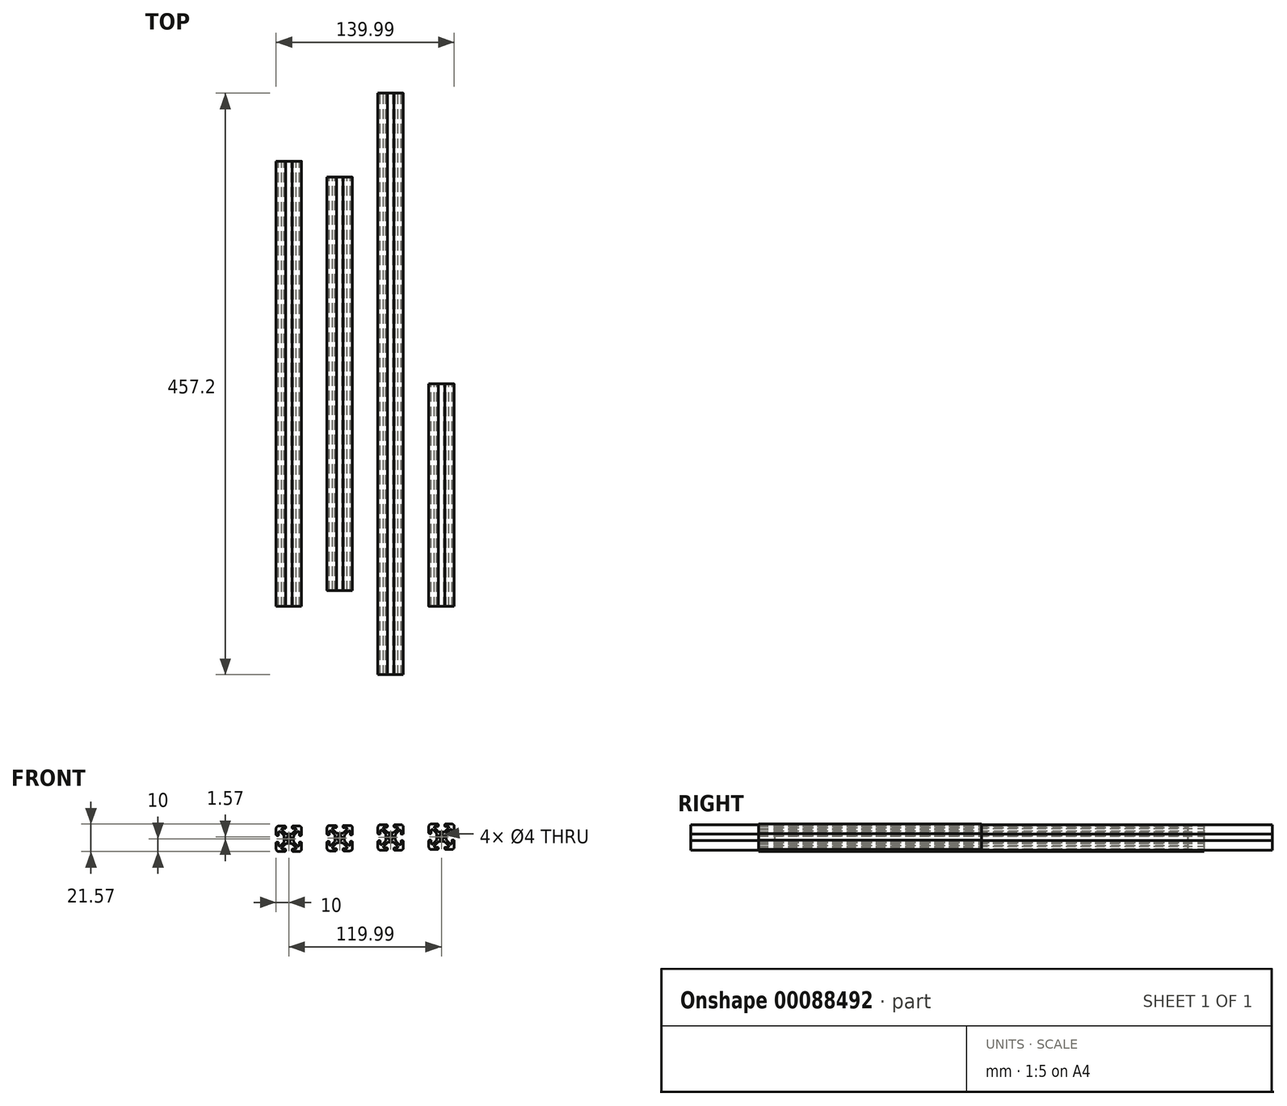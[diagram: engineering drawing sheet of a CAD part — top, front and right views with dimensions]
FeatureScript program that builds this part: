
annotation { "Feature Type Name" : "Feature", "Feature Type Description" : "" }
export const myFeature = defineFeature(function(context is Context, id is Id, definition is map)
    precondition{}
    {
        {
            var Q0;
            Q0=qCreatedBy(makeId("Front.planeOp"),FACE);
            var sketch = newSketch(context, id + "F0", { "sketchPlane" : qUnion([Q0])});
            skLineSegment(sketch, "E0.0.53", {"start": v(3.64, 0) * mm, "end": v(3.64, 1.13) * mm});
            skArc(sketch, "E0.0.54", {"start": v(3.64, 1.13) * mm, "mid": v(3.87, 2.28) * mm, "end": v(4.52, 3.25) * mm});
            skLineSegment(sketch, "E0.0.55", {"start": v(4.52, 3.25) * mm, "end": v(6.77, 5.5) * mm});
            skArc(sketch, "E0.0.56", {"start": v(6.77, 5.5) * mm, "mid": v(7.68, 5.68) * mm, "end": v(8.2, 4.9) * mm});
            skLineSegment(sketch, "E0.0.57", {"start": v(8.2, 4.9) * mm, "end": v(8.2, 2.8) * mm});
            skArc(sketch, "E0.0.58", {"start": v(8.2, 2.8) * mm, "mid": v(8.29, 2.59) * mm, "end": v(8.5, 2.5) * mm});
            skLineSegment(sketch, "E0.0.59", {"start": v(8.5, 2.5) * mm, "end": v(9.21, 2.5) * mm});
            skArc(sketch, "E0.0.60", {"start": v(9.21, 2.5) * mm, "mid": v(9.77, 2.73) * mm, "end": v(10, 3.29) * mm});
            skLineSegment(sketch, "E0.0.61", {"start": v(10, 3.29) * mm, "end": v(10, 7.99) * mm});
            skArc(sketch, "E0.0.62", {"start": v(10, 7.99) * mm, "mid": v(9.41, 9.41) * mm, "end": v(7.99, 10) * mm});
            skLineSegment(sketch, "E0.0.63", {"start": v(7.99, 10) * mm, "end": v(3.29, 10) * mm});
            skArc(sketch, "E0.0.64", {"start": v(3.29, 10) * mm, "mid": v(2.73, 9.77) * mm, "end": v(2.5, 9.21) * mm});
            skLineSegment(sketch, "E0.0.65", {"start": v(2.5, 9.21) * mm, "end": v(2.5, 8.5) * mm});
            skArc(sketch, "E0.0.66", {"start": v(2.5, 8.5) * mm, "mid": v(2.59, 8.29) * mm, "end": v(2.8, 8.2) * mm});
            skLineSegment(sketch, "E0.0.67", {"start": v(2.8, 8.2) * mm, "end": v(4.9, 8.2) * mm});
            skArc(sketch, "E0.0.68", {"start": v(4.9, 8.2) * mm, "mid": v(5.68, 7.68) * mm, "end": v(5.5, 6.77) * mm});
            skLineSegment(sketch, "E0.0.69", {"start": v(5.5, 6.77) * mm, "end": v(3.25, 4.52) * mm});
            skArc(sketch, "E0.0.70", {"start": v(3.25, 4.52) * mm, "mid": v(2.28, 3.87) * mm, "end": v(1.13, 3.64) * mm});
            skLineSegment(sketch, "E0.0.71", {"start": v(1.13, 3.64) * mm, "end": v(0, 3.64) * mm});
            skLineSegment(sketch, "E1", {"start": v(0, 0) * mm, "end": v(0, 10.71) * mm, "construction": true});
            skLineSegment(sketch, "E2", {"start": v(0, 0) * mm, "end": v(12.42, 0) * mm, "construction": true});
            skLineSegment(sketch, "E3", {"start": v(0, 0) * mm, "end": v(7.99, 7.99) * mm, "construction": true});
            skLineSegment(sketch, "E4.MirrorCS", {"start": v(8.5, -2.5) * mm, "end": v(9.21, -2.5) * mm});
            skArc(sketch, "E5.MirrorCS", {"start": v(8.2, -2.8) * mm, "mid": v(8.29, -2.59) * mm, "end": v(8.5, -2.5) * mm});
            skArc(sketch, "E6.MirrorCS", {"start": v(2.5, -8.5) * mm, "mid": v(2.59, -8.29) * mm, "end": v(2.8, -8.2) * mm});
            skLineSegment(sketch, "E7.MirrorCS", {"start": v(2.5, -9.21) * mm, "end": v(2.5, -8.5) * mm});
            skArc(sketch, "E8.MirrorCS", {"start": v(4.9, -8.2) * mm, "mid": v(5.68, -7.68) * mm, "end": v(5.5, -6.77) * mm});
            skArc(sketch, "E9.MirrorCS", {"start": v(3.64, -1.13) * mm, "mid": v(3.87, -2.28) * mm, "end": v(4.52, -3.25) * mm});
            skLineSegment(sketch, "E10.MirrorCS", {"start": v(10, -3.29) * mm, "end": v(10, -7.99) * mm});
            skArc(sketch, "E11.MirrorCS", {"start": v(3.25, -4.52) * mm, "mid": v(2.28, -3.87) * mm, "end": v(1.13, -3.64) * mm});
            skArc(sketch, "E12.MirrorCS", {"start": v(9.21, -2.5) * mm, "mid": v(9.77, -2.73) * mm, "end": v(10, -3.29) * mm});
            skLineSegment(sketch, "E13.MirrorCS", {"start": v(2.8, -8.2) * mm, "end": v(4.9, -8.2) * mm});
            skLineSegment(sketch, "E14.MirrorCS", {"start": v(4.52, -3.25) * mm, "end": v(6.77, -5.5) * mm});
            skLineSegment(sketch, "E15.MirrorCS", {"start": v(8.2, -4.9) * mm, "end": v(8.2, -2.8) * mm});
            skLineSegment(sketch, "E16.MirrorCS", {"start": v(3.64, 0) * mm, "end": v(3.64, -1.13) * mm});
            skLineSegment(sketch, "E17.MirrorCS", {"start": v(7.99, -10) * mm, "end": v(3.29, -10) * mm});
            skLineSegment(sketch, "E18.MirrorCS", {"start": v(5.5, -6.77) * mm, "end": v(3.25, -4.52) * mm});
            skArc(sketch, "E19.MirrorCS", {"start": v(6.77, -5.5) * mm, "mid": v(7.68, -5.68) * mm, "end": v(8.2, -4.9) * mm});
            skArc(sketch, "E20.MirrorCS", {"start": v(10, -7.99) * mm, "mid": v(9.41, -9.41) * mm, "end": v(7.99, -10) * mm});
            skArc(sketch, "E21.MirrorCS", {"start": v(3.29, -10) * mm, "mid": v(2.73, -9.77) * mm, "end": v(2.5, -9.21) * mm});
            skLineSegment(sketch, "E22.MirrorCS", {"start": v(1.13, -3.64) * mm, "end": v(0, -3.64) * mm});
            skLineSegment(sketch, "E23.MirrorCS", {"start": v(-2.5, 9.21) * mm, "end": v(-2.5, 8.5) * mm});
            skArc(sketch, "E24.MirrorCS", {"start": v(-8.2, -2.8) * mm, "mid": v(-8.29, -2.59) * mm, "end": v(-8.5, -2.5) * mm});
            skLineSegment(sketch, "E25.MirrorCS", {"start": v(-8.5, -2.5) * mm, "end": v(-9.21, -2.5) * mm});
            skArc(sketch, "E26.MirrorCS", {"start": v(-2.5, 8.5) * mm, "mid": v(-2.59, 8.29) * mm, "end": v(-2.8, 8.2) * mm});
            skLineSegment(sketch, "E27.MirrorCS", {"start": v(-3.64, 0) * mm, "end": v(-3.64, 1.13) * mm});
            skLineSegment(sketch, "E28.MirrorCS", {"start": v(-3.64, 0) * mm, "end": v(-3.64, -1.13) * mm});
            skArc(sketch, "E29.MirrorCS", {"start": v(-2.5, -8.5) * mm, "mid": v(-2.59, -8.29) * mm, "end": v(-2.8, -8.2) * mm});
            skLineSegment(sketch, "E30.MirrorCS", {"start": v(-2.5, -9.21) * mm, "end": v(-2.5, -8.5) * mm});
            skLineSegment(sketch, "E31.MirrorCS", {"start": v(-8.5, 2.5) * mm, "end": v(-9.21, 2.5) * mm});
            skArc(sketch, "E32.MirrorCS", {"start": v(-8.2, 2.8) * mm, "mid": v(-8.29, 2.59) * mm, "end": v(-8.5, 2.5) * mm});
            skLineSegment(sketch, "E33.MirrorCS", {"start": v(-1.13, -3.64) * mm, "end": v(0, -3.64) * mm});
            skLineSegment(sketch, "E34.MirrorCS", {"start": v(-1.13, 3.64) * mm, "end": v(0, 3.64) * mm});
            skArc(sketch, "E35.MirrorCS", {"start": v(-9.21, -2.5) * mm, "mid": v(-9.77, -2.73) * mm, "end": v(-10, -3.29) * mm});
            skLineSegment(sketch, "E36.MirrorCS", {"start": v(-4.52, 3.25) * mm, "end": v(-6.77, 5.5) * mm});
            skLineSegment(sketch, "E37.MirrorCS", {"start": v(-5.5, 6.77) * mm, "end": v(-3.25, 4.52) * mm});
            skLineSegment(sketch, "E38.MirrorCS", {"start": v(-8.2, 4.9) * mm, "end": v(-8.2, 2.8) * mm});
            skArc(sketch, "E39.MirrorCS", {"start": v(-6.77, 5.5) * mm, "mid": v(-7.68, 5.68) * mm, "end": v(-8.2, 4.9) * mm});
            skArc(sketch, "E40.MirrorCS", {"start": v(-4.9, -8.2) * mm, "mid": v(-5.68, -7.68) * mm, "end": v(-5.5, -6.77) * mm});
            skLineSegment(sketch, "E41.MirrorCS", {"start": v(-7.99, -10) * mm, "end": v(-3.29, -10) * mm});
            skArc(sketch, "E42.MirrorCS", {"start": v(-3.25, 4.52) * mm, "mid": v(-2.28, 3.87) * mm, "end": v(-1.13, 3.64) * mm});
            skArc(sketch, "E43.MirrorCS", {"start": v(-6.77, -5.5) * mm, "mid": v(-7.68, -5.68) * mm, "end": v(-8.2, -4.9) * mm});
            skLineSegment(sketch, "E44.MirrorCS", {"start": v(-2.8, -8.2) * mm, "end": v(-4.9, -8.2) * mm});
            skArc(sketch, "E45.MirrorCS", {"start": v(-3.25, -4.52) * mm, "mid": v(-2.28, -3.87) * mm, "end": v(-1.13, -3.64) * mm});
            skArc(sketch, "E46.MirrorCS", {"start": v(-3.64, -1.13) * mm, "mid": v(-3.87, -2.28) * mm, "end": v(-4.52, -3.25) * mm});
            skLineSegment(sketch, "E47.MirrorCS", {"start": v(-2.8, 8.2) * mm, "end": v(-4.9, 8.2) * mm});
            skArc(sketch, "E48.MirrorCS", {"start": v(-4.9, 8.2) * mm, "mid": v(-5.68, 7.68) * mm, "end": v(-5.5, 6.77) * mm});
            skLineSegment(sketch, "E49.MirrorCS", {"start": v(-10, -3.29) * mm, "end": v(-10, -7.99) * mm});
            skArc(sketch, "E50.MirrorCS", {"start": v(-3.29, -10) * mm, "mid": v(-2.73, -9.77) * mm, "end": v(-2.5, -9.21) * mm});
            skArc(sketch, "E51.MirrorCS", {"start": v(-10, -7.99) * mm, "mid": v(-9.41, -9.41) * mm, "end": v(-7.99, -10) * mm});
            skArc(sketch, "E52.MirrorCS", {"start": v(-3.29, 10) * mm, "mid": v(-2.73, 9.77) * mm, "end": v(-2.5, 9.21) * mm});
            skLineSegment(sketch, "E53.MirrorCS", {"start": v(-7.99, 10) * mm, "end": v(-3.29, 10) * mm});
            skArc(sketch, "E54.MirrorCS", {"start": v(-10, 7.99) * mm, "mid": v(-9.41, 9.41) * mm, "end": v(-7.99, 10) * mm});
            skLineSegment(sketch, "E55.MirrorCS", {"start": v(-8.2, -4.9) * mm, "end": v(-8.2, -2.8) * mm});
            skArc(sketch, "E56.MirrorCS", {"start": v(-3.64, 1.13) * mm, "mid": v(-3.87, 2.28) * mm, "end": v(-4.52, 3.25) * mm});
            skLineSegment(sketch, "E57.MirrorCS", {"start": v(-5.5, -6.77) * mm, "end": v(-3.25, -4.52) * mm});
            skLineSegment(sketch, "E58.MirrorCS", {"start": v(-10, 3.29) * mm, "end": v(-10, 7.99) * mm});
            skArc(sketch, "E59.MirrorCS", {"start": v(-9.21, 2.5) * mm, "mid": v(-9.77, 2.73) * mm, "end": v(-10, 3.29) * mm});
            skLineSegment(sketch, "E60.MirrorCS", {"start": v(-4.52, -3.25) * mm, "end": v(-6.77, -5.5) * mm});
            skCircle(sketch, "E61", {"center": v(0, 0) * mm, "radius": 2 * mm});
            skArc(sketch, "E62.1.0.0", {"start": v(44.9, -7.68) * mm, "mid": v(45.68, -7.16) * mm, "end": v(45.5, -6.25) * mm});
            skArc(sketch, "E62.1.0.1", {"start": v(36.35, 1.65) * mm, "mid": v(36.12, 2.8) * mm, "end": v(35.47, 3.77) * mm});
            skLineSegment(sketch, "E62.1.0.2", {"start": v(40, 0.52) * mm, "end": v(40, 11.24) * mm, "construction": true});
            skLineSegment(sketch, "E62.1.0.3", {"start": v(30, -2.76) * mm, "end": v(30, -7.46) * mm});
            skLineSegment(sketch, "E62.1.0.4", {"start": v(47.98, -9.48) * mm, "end": v(43.28, -9.48) * mm});
            skLineSegment(sketch, "E62.1.0.5", {"start": v(32, -9.48) * mm, "end": v(36.7, -9.48) * mm});
            skArc(sketch, "E62.1.0.6", {"start": v(43.64, -0.6) * mm, "mid": v(43.87, -1.75) * mm, "end": v(44.52, -2.73) * mm});
            skLineSegment(sketch, "E62.1.0.7", {"start": v(34.5, -6.25) * mm, "end": v(36.75, -4) * mm});
            skLineSegment(sketch, "E62.1.0.8", {"start": v(40, 0.52) * mm, "end": v(52.42, 0.52) * mm, "construction": true});
            skArc(sketch, "E62.1.0.9", {"start": v(33.22, -4.98) * mm, "mid": v(32.31, -5.16) * mm, "end": v(31.8, -4.39) * mm});
            skLineSegment(sketch, "E62.1.0.10", {"start": v(45.5, -6.25) * mm, "end": v(43.25, -4) * mm});
            skArc(sketch, "E62.1.0.11", {"start": v(43.25, -4) * mm, "mid": v(42.27, -3.35) * mm, "end": v(41.13, -3.12) * mm});
            skArc(sketch, "E62.1.0.12", {"start": v(36.75, 5.05) * mm, "mid": v(37.72, 4.4) * mm, "end": v(38.87, 4.17) * mm});
            skLineSegment(sketch, "E62.1.0.13", {"start": v(50, -2.76) * mm, "end": v(50, -7.46) * mm});
            skLineSegment(sketch, "E62.1.0.14", {"start": v(30, 3.81) * mm, "end": v(30, 8.51) * mm});
            skLineSegment(sketch, "E62.1.0.15", {"start": v(40, 0.52) * mm, "end": v(47.98, 8.51) * mm, "construction": true});
            skLineSegment(sketch, "E62.1.0.16", {"start": v(35.47, -2.73) * mm, "end": v(33.22, -4.98) * mm});
            skArc(sketch, "E62.1.0.17", {"start": v(30, -7.46) * mm, "mid": v(30.59, -8.89) * mm, "end": v(32, -9.48) * mm});
            skLineSegment(sketch, "E62.1.0.18", {"start": v(37.2, -7.68) * mm, "end": v(35.09, -7.68) * mm});
            skCircle(sketch, "E62.1.0.19", {"center": v(40, 0.52) * mm, "radius": 2 * mm});
            skArc(sketch, "E62.1.0.20", {"start": v(36.75, -4) * mm, "mid": v(37.72, -3.35) * mm, "end": v(38.87, -3.12) * mm});
            skLineSegment(sketch, "E62.1.0.21", {"start": v(35.47, 3.77) * mm, "end": v(33.22, 6.02) * mm});
            skArc(sketch, "E62.1.0.22", {"start": v(50, -7.46) * mm, "mid": v(49.4, -8.89) * mm, "end": v(47.98, -9.48) * mm});
            skLineSegment(sketch, "E62.1.0.23", {"start": v(42.8, -7.68) * mm, "end": v(44.9, -7.68) * mm});
            skLineSegment(sketch, "E62.1.0.24", {"start": v(42.8, 8.72) * mm, "end": v(44.9, 8.72) * mm});
            skArc(sketch, "E62.1.0.25", {"start": v(44.9, 8.72) * mm, "mid": v(45.68, 8.2) * mm, "end": v(45.5, 7.3) * mm});
            skArc(sketch, "E62.1.0.26", {"start": v(43.64, 1.65) * mm, "mid": v(43.87, 2.8) * mm, "end": v(44.52, 3.77) * mm});
            skLineSegment(sketch, "E62.1.0.27", {"start": v(44.52, 3.77) * mm, "end": v(46.77, 6.02) * mm});
            skLineSegment(sketch, "E62.1.0.28", {"start": v(48.2, 5.43) * mm, "end": v(48.2, 3.33) * mm});
            skLineSegment(sketch, "E62.1.0.29", {"start": v(50, 3.81) * mm, "end": v(50, 8.51) * mm});
            skArc(sketch, "E62.1.0.30", {"start": v(50, 8.51) * mm, "mid": v(49.4, 9.93) * mm, "end": v(47.98, 10.52) * mm});
            skLineSegment(sketch, "E62.1.0.31", {"start": v(47.98, 10.52) * mm, "end": v(43.28, 10.52) * mm});
            skLineSegment(sketch, "E62.1.0.32", {"start": v(34.5, 7.3) * mm, "end": v(36.75, 5.05) * mm});
            skLineSegment(sketch, "E62.1.0.33", {"start": v(32, 10.52) * mm, "end": v(36.7, 10.52) * mm});
            skLineSegment(sketch, "E62.1.0.34", {"start": v(45.5, 7.3) * mm, "end": v(43.25, 5.05) * mm});
            skLineSegment(sketch, "E62.1.0.35", {"start": v(44.52, -2.73) * mm, "end": v(46.77, -4.98) * mm});
            skLineSegment(sketch, "E62.1.0.36", {"start": v(31.8, 5.43) * mm, "end": v(31.8, 3.33) * mm});
            skArc(sketch, "E62.1.0.37", {"start": v(30, 8.51) * mm, "mid": v(30.59, 9.93) * mm, "end": v(32, 10.52) * mm});
            skArc(sketch, "E62.1.0.38", {"start": v(43.25, 5.05) * mm, "mid": v(42.27, 4.4) * mm, "end": v(41.13, 4.17) * mm});
            skLineSegment(sketch, "E62.1.0.39", {"start": v(48.2, -4.39) * mm, "end": v(48.2, -2.28) * mm});
            skArc(sketch, "E62.1.0.40", {"start": v(33.22, 6.02) * mm, "mid": v(32.31, 6.2) * mm, "end": v(31.8, 5.43) * mm});
            skLineSegment(sketch, "E62.1.0.41", {"start": v(31.8, -4.39) * mm, "end": v(31.8, -2.28) * mm});
            skArc(sketch, "E62.1.0.42", {"start": v(36.35, -0.6) * mm, "mid": v(36.12, -1.75) * mm, "end": v(35.47, -2.73) * mm});
            skLineSegment(sketch, "E62.1.0.43", {"start": v(37.2, 8.72) * mm, "end": v(35.09, 8.72) * mm});
            skArc(sketch, "E62.1.0.44", {"start": v(35.09, -7.68) * mm, "mid": v(34.32, -7.16) * mm, "end": v(34.5, -6.25) * mm});
            skArc(sketch, "E62.1.0.45", {"start": v(31.8, -2.28) * mm, "mid": v(31.7, -2.07) * mm, "end": v(31.5, -1.98) * mm});
            skLineSegment(sketch, "E62.1.0.46", {"start": v(38.87, -3.12) * mm, "end": v(40, -3.12) * mm});
            skLineSegment(sketch, "E62.1.0.47", {"start": v(31.5, -1.98) * mm, "end": v(30.78, -1.98) * mm});
            skArc(sketch, "E62.1.0.48", {"start": v(30.78, 3.02) * mm, "mid": v(30.23, 3.25) * mm, "end": v(30, 3.81) * mm});
            skArc(sketch, "E62.1.0.49", {"start": v(36.7, -9.48) * mm, "mid": v(37.27, -9.25) * mm, "end": v(37.5, -8.69) * mm});
            skLineSegment(sketch, "E62.1.0.50", {"start": v(38.87, 4.17) * mm, "end": v(40, 4.17) * mm});
            skLineSegment(sketch, "E62.1.0.51", {"start": v(36.35, 0.52) * mm, "end": v(36.35, 1.65) * mm});
            skArc(sketch, "E62.1.0.52", {"start": v(30.78, -1.98) * mm, "mid": v(30.23, -2.2) * mm, "end": v(30, -2.76) * mm});
            skLineSegment(sketch, "E62.1.0.53", {"start": v(36.35, 0.52) * mm, "end": v(36.35, -0.6) * mm});
            skArc(sketch, "E62.1.0.54", {"start": v(46.77, -4.98) * mm, "mid": v(47.68, -5.16) * mm, "end": v(48.2, -4.39) * mm});
            skArc(sketch, "E62.1.0.55", {"start": v(49.2, -1.98) * mm, "mid": v(49.77, -2.2) * mm, "end": v(50, -2.76) * mm});
            skArc(sketch, "E62.1.0.56", {"start": v(36.7, 10.52) * mm, "mid": v(37.27, 10.3) * mm, "end": v(37.5, 9.74) * mm});
            skArc(sketch, "E62.1.0.57", {"start": v(37.5, -7.98) * mm, "mid": v(37.4, -7.77) * mm, "end": v(37.2, -7.68) * mm});
            skLineSegment(sketch, "E62.1.0.58", {"start": v(43.64, 0.52) * mm, "end": v(43.64, 1.65) * mm});
            skArc(sketch, "E62.1.0.59", {"start": v(46.77, 6.02) * mm, "mid": v(47.68, 6.2) * mm, "end": v(48.2, 5.43) * mm});
            skArc(sketch, "E62.1.0.60", {"start": v(48.2, 3.33) * mm, "mid": v(48.29, 3.11) * mm, "end": v(48.5, 3.02) * mm});
            skLineSegment(sketch, "E62.1.0.61", {"start": v(48.5, 3.02) * mm, "end": v(49.2, 3.02) * mm});
            skArc(sketch, "E62.1.0.62", {"start": v(49.2, 3.02) * mm, "mid": v(49.77, 3.25) * mm, "end": v(50, 3.81) * mm});
            skArc(sketch, "E62.1.0.63", {"start": v(43.28, 10.52) * mm, "mid": v(42.73, 10.3) * mm, "end": v(42.5, 9.74) * mm});
            skArc(sketch, "E62.1.0.64", {"start": v(43.28, -9.48) * mm, "mid": v(42.73, -9.25) * mm, "end": v(42.5, -8.69) * mm});
            skArc(sketch, "E62.1.0.65", {"start": v(48.2, -2.28) * mm, "mid": v(48.29, -2.07) * mm, "end": v(48.5, -1.98) * mm});
            skLineSegment(sketch, "E62.1.0.66", {"start": v(37.5, -8.69) * mm, "end": v(37.5, -7.98) * mm});
            skLineSegment(sketch, "E62.1.0.67", {"start": v(41.13, -3.12) * mm, "end": v(40, -3.12) * mm});
            skArc(sketch, "E62.1.0.68", {"start": v(42.5, -7.98) * mm, "mid": v(42.59, -7.77) * mm, "end": v(42.8, -7.68) * mm});
            skLineSegment(sketch, "E62.1.0.69", {"start": v(31.5, 3.02) * mm, "end": v(30.78, 3.02) * mm});
            skLineSegment(sketch, "E62.1.0.70", {"start": v(42.5, -8.69) * mm, "end": v(42.5, -7.98) * mm});
            skLineSegment(sketch, "E62.1.0.71", {"start": v(41.13, 4.17) * mm, "end": v(40, 4.17) * mm});
            skArc(sketch, "E62.1.0.72", {"start": v(35.09, 8.72) * mm, "mid": v(34.32, 8.2) * mm, "end": v(34.5, 7.3) * mm});
            skArc(sketch, "E62.1.0.73", {"start": v(31.8, 3.33) * mm, "mid": v(31.7, 3.11) * mm, "end": v(31.5, 3.02) * mm});
            skLineSegment(sketch, "E62.1.0.74", {"start": v(43.64, 0.52) * mm, "end": v(43.64, -0.6) * mm});
            skArc(sketch, "E62.1.0.75", {"start": v(37.5, 9.03) * mm, "mid": v(37.4, 8.81) * mm, "end": v(37.2, 8.72) * mm});
            skLineSegment(sketch, "E62.1.0.76", {"start": v(48.5, -1.98) * mm, "end": v(49.2, -1.98) * mm});
            skArc(sketch, "E62.1.0.77", {"start": v(42.5, 9.03) * mm, "mid": v(42.59, 8.81) * mm, "end": v(42.8, 8.72) * mm});
            skLineSegment(sketch, "E62.1.0.78", {"start": v(42.5, 9.74) * mm, "end": v(42.5, 9.03) * mm});
            skLineSegment(sketch, "E62.1.0.79", {"start": v(37.5, 9.74) * mm, "end": v(37.5, 9.03) * mm});
            skArc(sketch, "E62.2.0.0", {"start": v(84.9, -7.15) * mm, "mid": v(85.67, -6.64) * mm, "end": v(85.5, -5.73) * mm});
            skArc(sketch, "E62.2.0.1", {"start": v(76.35, 2.18) * mm, "mid": v(76.12, 3.32) * mm, "end": v(75.47, 4.3) * mm});
            skLineSegment(sketch, "E62.2.0.2", {"start": v(80, 1.05) * mm, "end": v(80, 11.76) * mm, "construction": true});
            skLineSegment(sketch, "E62.2.0.3", {"start": v(70, -2.24) * mm, "end": v(70, -6.94) * mm});
            skLineSegment(sketch, "E62.2.0.4", {"start": v(87.98, -8.95) * mm, "end": v(83.28, -8.95) * mm});
            skLineSegment(sketch, "E62.2.0.5", {"start": v(72, -8.95) * mm, "end": v(76.7, -8.95) * mm});
            skArc(sketch, "E62.2.0.6", {"start": v(83.64, -0.08) * mm, "mid": v(83.87, -1.23) * mm, "end": v(84.52, -2.2) * mm});
            skLineSegment(sketch, "E62.2.0.7", {"start": v(74.5, -5.73) * mm, "end": v(76.74, -3.48) * mm});
            skLineSegment(sketch, "E62.2.0.8", {"start": v(80, 1.05) * mm, "end": v(92.41, 1.05) * mm, "construction": true});
            skArc(sketch, "E62.2.0.9", {"start": v(73.22, -4.45) * mm, "mid": v(72.3, -4.63) * mm, "end": v(71.8, -3.86) * mm});
            skLineSegment(sketch, "E62.2.0.10", {"start": v(85.5, -5.73) * mm, "end": v(83.24, -3.48) * mm});
            skArc(sketch, "E62.2.0.11", {"start": v(83.24, -3.48) * mm, "mid": v(82.27, -2.83) * mm, "end": v(81.12, -2.6) * mm});
            skArc(sketch, "E62.2.0.12", {"start": v(76.74, 5.57) * mm, "mid": v(77.72, 4.92) * mm, "end": v(78.86, 4.7) * mm});
            skLineSegment(sketch, "E62.2.0.13", {"start": v(90, -2.24) * mm, "end": v(90, -6.94) * mm});
            skLineSegment(sketch, "E62.2.0.14", {"start": v(70, 4.33) * mm, "end": v(70, 9.03) * mm});
            skLineSegment(sketch, "E62.2.0.15", {"start": v(80, 1.05) * mm, "end": v(87.98, 9.03) * mm, "construction": true});
            skLineSegment(sketch, "E62.2.0.16", {"start": v(75.47, -2.2) * mm, "end": v(73.22, -4.45) * mm});
            skArc(sketch, "E62.2.0.17", {"start": v(70, -6.94) * mm, "mid": v(70.58, -8.36) * mm, "end": v(72, -8.95) * mm});
            skLineSegment(sketch, "E62.2.0.18", {"start": v(77.19, -7.15) * mm, "end": v(75.08, -7.15) * mm});
            skCircle(sketch, "E62.2.0.19", {"center": v(80, 1.05) * mm, "radius": 2 * mm});
            skArc(sketch, "E62.2.0.20", {"start": v(76.74, -3.48) * mm, "mid": v(77.72, -2.83) * mm, "end": v(78.86, -2.6) * mm});
            skLineSegment(sketch, "E62.2.0.21", {"start": v(75.47, 4.3) * mm, "end": v(73.22, 6.55) * mm});
            skArc(sketch, "E62.2.0.22", {"start": v(90, -6.94) * mm, "mid": v(89.4, -8.36) * mm, "end": v(87.98, -8.95) * mm});
            skLineSegment(sketch, "E62.2.0.23", {"start": v(82.8, -7.15) * mm, "end": v(84.9, -7.15) * mm});
            skLineSegment(sketch, "E62.2.0.24", {"start": v(82.8, 9.25) * mm, "end": v(84.9, 9.25) * mm});
            skArc(sketch, "E62.2.0.25", {"start": v(84.9, 9.25) * mm, "mid": v(85.67, 8.73) * mm, "end": v(85.5, 7.82) * mm});
            skArc(sketch, "E62.2.0.26", {"start": v(83.64, 2.18) * mm, "mid": v(83.87, 3.32) * mm, "end": v(84.52, 4.3) * mm});
            skLineSegment(sketch, "E62.2.0.27", {"start": v(84.52, 4.3) * mm, "end": v(86.77, 6.55) * mm});
            skLineSegment(sketch, "E62.2.0.28", {"start": v(88.2, 5.96) * mm, "end": v(88.2, 3.85) * mm});
            skLineSegment(sketch, "E62.2.0.29", {"start": v(90, 4.33) * mm, "end": v(90, 9.03) * mm});
            skArc(sketch, "E62.2.0.30", {"start": v(90, 9.03) * mm, "mid": v(89.4, 10.46) * mm, "end": v(87.98, 11.05) * mm});
            skLineSegment(sketch, "E62.2.0.31", {"start": v(87.98, 11.05) * mm, "end": v(83.28, 11.05) * mm});
            skLineSegment(sketch, "E62.2.0.32", {"start": v(74.5, 7.82) * mm, "end": v(76.74, 5.57) * mm});
            skLineSegment(sketch, "E62.2.0.33", {"start": v(72, 11.05) * mm, "end": v(76.7, 11.05) * mm});
            skLineSegment(sketch, "E62.2.0.34", {"start": v(85.5, 7.82) * mm, "end": v(83.24, 5.57) * mm});
            skLineSegment(sketch, "E62.2.0.35", {"start": v(84.52, -2.2) * mm, "end": v(86.77, -4.45) * mm});
            skLineSegment(sketch, "E62.2.0.36", {"start": v(71.8, 5.96) * mm, "end": v(71.8, 3.85) * mm});
            skArc(sketch, "E62.2.0.37", {"start": v(70, 9.03) * mm, "mid": v(70.58, 10.46) * mm, "end": v(72, 11.05) * mm});
            skArc(sketch, "E62.2.0.38", {"start": v(83.24, 5.57) * mm, "mid": v(82.27, 4.92) * mm, "end": v(81.12, 4.7) * mm});
            skLineSegment(sketch, "E62.2.0.39", {"start": v(88.2, -3.86) * mm, "end": v(88.2, -1.76) * mm});
            skArc(sketch, "E62.2.0.40", {"start": v(73.22, 6.55) * mm, "mid": v(72.3, 6.73) * mm, "end": v(71.8, 5.96) * mm});
            skLineSegment(sketch, "E62.2.0.41", {"start": v(71.8, -3.86) * mm, "end": v(71.8, -1.76) * mm});
            skArc(sketch, "E62.2.0.42", {"start": v(76.35, -0.08) * mm, "mid": v(76.12, -1.23) * mm, "end": v(75.47, -2.2) * mm});
            skLineSegment(sketch, "E62.2.0.43", {"start": v(77.19, 9.25) * mm, "end": v(75.08, 9.25) * mm});
            skArc(sketch, "E62.2.0.44", {"start": v(75.08, -7.15) * mm, "mid": v(74.31, -6.64) * mm, "end": v(74.5, -5.73) * mm});
            skArc(sketch, "E62.2.0.45", {"start": v(71.8, -1.76) * mm, "mid": v(71.7, -1.54) * mm, "end": v(71.49, -1.45) * mm});
            skLineSegment(sketch, "E62.2.0.46", {"start": v(78.86, -2.6) * mm, "end": v(80, -2.6) * mm});
            skLineSegment(sketch, "E62.2.0.47", {"start": v(71.49, -1.45) * mm, "end": v(70.78, -1.45) * mm});
            skArc(sketch, "E62.2.0.48", {"start": v(70.78, 3.55) * mm, "mid": v(70.22, 3.78) * mm, "end": v(70, 4.33) * mm});
            skArc(sketch, "E62.2.0.49", {"start": v(76.7, -8.95) * mm, "mid": v(77.26, -8.72) * mm, "end": v(77.5, -8.17) * mm});
            skLineSegment(sketch, "E62.2.0.50", {"start": v(78.86, 4.7) * mm, "end": v(80, 4.7) * mm});
            skLineSegment(sketch, "E62.2.0.51", {"start": v(76.35, 1.05) * mm, "end": v(76.35, 2.18) * mm});
            skArc(sketch, "E62.2.0.52", {"start": v(70.78, -1.45) * mm, "mid": v(70.22, -1.68) * mm, "end": v(70, -2.24) * mm});
            skLineSegment(sketch, "E62.2.0.53", {"start": v(76.35, 1.05) * mm, "end": v(76.35, -0.08) * mm});
            skArc(sketch, "E62.2.0.54", {"start": v(86.77, -4.45) * mm, "mid": v(87.68, -4.63) * mm, "end": v(88.2, -3.86) * mm});
            skArc(sketch, "E62.2.0.55", {"start": v(89.2, -1.45) * mm, "mid": v(89.76, -1.68) * mm, "end": v(90, -2.24) * mm});
            skArc(sketch, "E62.2.0.56", {"start": v(76.7, 11.05) * mm, "mid": v(77.26, 10.82) * mm, "end": v(77.5, 10.26) * mm});
            skArc(sketch, "E62.2.0.57", {"start": v(77.5, -7.46) * mm, "mid": v(77.4, -7.24) * mm, "end": v(77.19, -7.15) * mm});
            skLineSegment(sketch, "E62.2.0.58", {"start": v(83.64, 1.05) * mm, "end": v(83.64, 2.18) * mm});
            skArc(sketch, "E62.2.0.59", {"start": v(86.77, 6.55) * mm, "mid": v(87.68, 6.73) * mm, "end": v(88.2, 5.96) * mm});
            skArc(sketch, "E62.2.0.60", {"start": v(88.2, 3.85) * mm, "mid": v(88.28, 3.64) * mm, "end": v(88.5, 3.55) * mm});
            skLineSegment(sketch, "E62.2.0.61", {"start": v(88.5, 3.55) * mm, "end": v(89.2, 3.55) * mm});
            skArc(sketch, "E62.2.0.62", {"start": v(89.2, 3.55) * mm, "mid": v(89.76, 3.78) * mm, "end": v(90, 4.33) * mm});
            skArc(sketch, "E62.2.0.63", {"start": v(83.28, 11.05) * mm, "mid": v(82.72, 10.82) * mm, "end": v(82.5, 10.26) * mm});
            skArc(sketch, "E62.2.0.64", {"start": v(83.28, -8.95) * mm, "mid": v(82.72, -8.72) * mm, "end": v(82.5, -8.17) * mm});
            skArc(sketch, "E62.2.0.65", {"start": v(88.2, -1.76) * mm, "mid": v(88.28, -1.54) * mm, "end": v(88.5, -1.45) * mm});
            skLineSegment(sketch, "E62.2.0.66", {"start": v(77.5, -8.17) * mm, "end": v(77.5, -7.46) * mm});
            skLineSegment(sketch, "E62.2.0.67", {"start": v(81.12, -2.6) * mm, "end": v(80, -2.6) * mm});
            skArc(sketch, "E62.2.0.68", {"start": v(82.5, -7.46) * mm, "mid": v(82.58, -7.24) * mm, "end": v(82.8, -7.15) * mm});
            skLineSegment(sketch, "E62.2.0.69", {"start": v(71.49, 3.55) * mm, "end": v(70.78, 3.55) * mm});
            skLineSegment(sketch, "E62.2.0.70", {"start": v(82.5, -8.17) * mm, "end": v(82.5, -7.46) * mm});
            skLineSegment(sketch, "E62.2.0.71", {"start": v(81.12, 4.7) * mm, "end": v(80, 4.7) * mm});
            skArc(sketch, "E62.2.0.72", {"start": v(75.08, 9.25) * mm, "mid": v(74.31, 8.73) * mm, "end": v(74.5, 7.82) * mm});
            skArc(sketch, "E62.2.0.73", {"start": v(71.8, 3.85) * mm, "mid": v(71.7, 3.64) * mm, "end": v(71.49, 3.55) * mm});
            skLineSegment(sketch, "E62.2.0.74", {"start": v(83.64, 1.05) * mm, "end": v(83.64, -0.08) * mm});
            skArc(sketch, "E62.2.0.75", {"start": v(77.5, 9.55) * mm, "mid": v(77.4, 9.34) * mm, "end": v(77.19, 9.25) * mm});
            skLineSegment(sketch, "E62.2.0.76", {"start": v(88.5, -1.45) * mm, "end": v(89.2, -1.45) * mm});
            skArc(sketch, "E62.2.0.77", {"start": v(82.5, 9.55) * mm, "mid": v(82.58, 9.34) * mm, "end": v(82.8, 9.25) * mm});
            skLineSegment(sketch, "E62.2.0.78", {"start": v(82.5, 10.26) * mm, "end": v(82.5, 9.55) * mm});
            skLineSegment(sketch, "E62.2.0.79", {"start": v(77.5, 10.26) * mm, "end": v(77.5, 9.55) * mm});
            skLineSegment(sketch, "E62.direction1", {"start": v(-7.99, -10) * mm, "end": v(32, -9.48) * mm, "construction": true});
            skArc(sketch, "E63.0.3.0", {"start": v(124.9, -6.63) * mm, "mid": v(125.67, -6.11) * mm, "end": v(125.49, -5.2) * mm});
            skArc(sketch, "E63.4.3.0", {"start": v(116.34, 2.7) * mm, "mid": v(116.12, 3.85) * mm, "end": v(115.47, 4.82) * mm});
            skLineSegment(sketch, "E63.8.3.0", {"start": v(119.99, 1.57) * mm, "end": v(119.99, 12.28) * mm, "construction": true});
            skLineSegment(sketch, "E63.11.3.0", {"start": v(109.99, -1.72) * mm, "end": v(109.99, -6.42) * mm});
            skLineSegment(sketch, "E63.14.3.0", {"start": v(127.98, -8.43) * mm, "end": v(123.28, -8.43) * mm});
            skLineSegment(sketch, "E63.17.3.0", {"start": v(112, -8.43) * mm, "end": v(116.7, -8.43) * mm});
            skArc(sketch, "E63.20.3.0", {"start": v(123.63, 0.44) * mm, "mid": v(123.86, -0.7) * mm, "end": v(124.51, -1.68) * mm});
            skLineSegment(sketch, "E63.24.3.0", {"start": v(114.49, -5.2) * mm, "end": v(116.74, -2.95) * mm});
            skLineSegment(sketch, "E63.27.3.0", {"start": v(119.99, 1.57) * mm, "end": v(132.4, 1.57) * mm, "construction": true});
            skArc(sketch, "E63.30.3.0", {"start": v(113.22, -3.93) * mm, "mid": v(112.3, -4.11) * mm, "end": v(111.79, -3.34) * mm});
            skLineSegment(sketch, "E63.34.3.0", {"start": v(125.49, -5.2) * mm, "end": v(123.24, -2.95) * mm});
            skArc(sketch, "E63.37.3.0", {"start": v(123.24, -2.95) * mm, "mid": v(122.27, -2.3) * mm, "end": v(121.12, -2.07) * mm});
            skArc(sketch, "E63.41.3.0", {"start": v(116.74, 6.1) * mm, "mid": v(117.71, 5.44) * mm, "end": v(118.86, 5.21) * mm});
            skLineSegment(sketch, "E63.45.3.0", {"start": v(129.99, -1.72) * mm, "end": v(129.99, -6.42) * mm});
            skLineSegment(sketch, "E63.48.3.0", {"start": v(109.99, 4.86) * mm, "end": v(109.99, 9.56) * mm});
            skLineSegment(sketch, "E63.51.3.0", {"start": v(119.99, 1.57) * mm, "end": v(127.98, 9.56) * mm, "construction": true});
            skLineSegment(sketch, "E63.54.3.0", {"start": v(115.47, -1.68) * mm, "end": v(113.22, -3.93) * mm});
            skArc(sketch, "E63.57.3.0", {"start": v(109.99, -6.42) * mm, "mid": v(110.58, -7.84) * mm, "end": v(112, -8.43) * mm});
            skLineSegment(sketch, "E63.61.3.0", {"start": v(117.18, -6.63) * mm, "end": v(115.08, -6.63) * mm});
            skCircle(sketch, "E63.64.3.0", {"center": v(119.99, 1.57) * mm, "radius": 2 * mm});
            skArc(sketch, "E63.66.3.0", {"start": v(116.74, -2.95) * mm, "mid": v(117.71, -2.3) * mm, "end": v(118.86, -2.07) * mm});
            skLineSegment(sketch, "E63.70.3.0", {"start": v(115.47, 4.82) * mm, "end": v(113.22, 7.07) * mm});
            skArc(sketch, "E63.73.3.0", {"start": v(129.99, -6.42) * mm, "mid": v(129.4, -7.84) * mm, "end": v(127.98, -8.43) * mm});
            skLineSegment(sketch, "E63.77.3.0", {"start": v(122.8, -6.63) * mm, "end": v(124.9, -6.63) * mm});
            skLineSegment(sketch, "E63.80.3.0", {"start": v(122.8, 9.77) * mm, "end": v(124.9, 9.77) * mm});
            skArc(sketch, "E63.83.3.0", {"start": v(124.9, 9.77) * mm, "mid": v(125.67, 9.25) * mm, "end": v(125.49, 8.34) * mm});
            skArc(sketch, "E63.87.3.0", {"start": v(123.63, 2.7) * mm, "mid": v(123.86, 3.85) * mm, "end": v(124.51, 4.82) * mm});
            skLineSegment(sketch, "E63.91.3.0", {"start": v(124.51, 4.82) * mm, "end": v(126.76, 7.07) * mm});
            skLineSegment(sketch, "E63.94.3.0", {"start": v(128.19, 6.48) * mm, "end": v(128.19, 4.37) * mm});
            skLineSegment(sketch, "E63.97.3.0", {"start": v(129.99, 4.86) * mm, "end": v(129.99, 9.56) * mm});
            skArc(sketch, "E63.100.3.0", {"start": v(129.99, 9.56) * mm, "mid": v(129.4, 10.98) * mm, "end": v(127.98, 11.57) * mm});
            skLineSegment(sketch, "E63.104.3.0", {"start": v(127.98, 11.57) * mm, "end": v(123.28, 11.57) * mm});
            skLineSegment(sketch, "E63.107.3.0", {"start": v(114.49, 8.34) * mm, "end": v(116.74, 6.1) * mm});
            skLineSegment(sketch, "E63.110.3.0", {"start": v(112, 11.57) * mm, "end": v(116.7, 11.57) * mm});
            skLineSegment(sketch, "E63.113.3.0", {"start": v(125.49, 8.34) * mm, "end": v(123.24, 6.1) * mm});
            skLineSegment(sketch, "E63.116.3.0", {"start": v(124.51, -1.68) * mm, "end": v(126.76, -3.93) * mm});
            skLineSegment(sketch, "E63.119.3.0", {"start": v(111.79, 6.48) * mm, "end": v(111.79, 4.37) * mm});
            skArc(sketch, "E63.122.3.0", {"start": v(109.99, 9.56) * mm, "mid": v(110.58, 10.98) * mm, "end": v(112, 11.57) * mm});
            skArc(sketch, "E63.126.3.0", {"start": v(123.24, 6.1) * mm, "mid": v(122.27, 5.44) * mm, "end": v(121.12, 5.21) * mm});
            skLineSegment(sketch, "E63.130.3.0", {"start": v(128.19, -3.34) * mm, "end": v(128.19, -1.23) * mm});
            skArc(sketch, "E63.133.3.0", {"start": v(113.22, 7.07) * mm, "mid": v(112.3, 7.25) * mm, "end": v(111.79, 6.48) * mm});
            skLineSegment(sketch, "E63.137.3.0", {"start": v(111.79, -3.34) * mm, "end": v(111.79, -1.23) * mm});
            skArc(sketch, "E63.140.3.0", {"start": v(116.34, 0.44) * mm, "mid": v(116.12, -0.7) * mm, "end": v(115.47, -1.68) * mm});
            skLineSegment(sketch, "E63.144.3.0", {"start": v(117.18, 9.77) * mm, "end": v(115.08, 9.77) * mm});
            skArc(sketch, "E63.147.3.0", {"start": v(115.08, -6.63) * mm, "mid": v(114.3, -6.11) * mm, "end": v(114.49, -5.2) * mm});
            skArc(sketch, "E63.151.3.0", {"start": v(111.79, -1.23) * mm, "mid": v(111.7, -1.02) * mm, "end": v(111.48, -0.93) * mm});
            skLineSegment(sketch, "E63.155.3.0", {"start": v(118.86, -2.07) * mm, "end": v(119.99, -2.07) * mm});
            skLineSegment(sketch, "E63.158.3.0", {"start": v(111.48, -0.93) * mm, "end": v(110.78, -0.93) * mm});
            skArc(sketch, "E63.161.3.0", {"start": v(110.78, 4.07) * mm, "mid": v(110.22, 4.3) * mm, "end": v(109.99, 4.86) * mm});
            skArc(sketch, "E63.165.3.0", {"start": v(116.7, -8.43) * mm, "mid": v(117.26, -8.2) * mm, "end": v(117.49, -7.64) * mm});
            skLineSegment(sketch, "E63.169.3.0", {"start": v(118.86, 5.21) * mm, "end": v(119.99, 5.21) * mm});
            skLineSegment(sketch, "E63.172.3.0", {"start": v(116.34, 1.57) * mm, "end": v(116.34, 2.7) * mm});
            skArc(sketch, "E63.175.3.0", {"start": v(110.78, -0.93) * mm, "mid": v(110.22, -1.16) * mm, "end": v(109.99, -1.72) * mm});
            skLineSegment(sketch, "E63.179.3.0", {"start": v(116.34, 1.57) * mm, "end": v(116.34, 0.44) * mm});
            skArc(sketch, "E63.182.3.0", {"start": v(126.76, -3.93) * mm, "mid": v(127.67, -4.11) * mm, "end": v(128.19, -3.34) * mm});
            skArc(sketch, "E63.186.3.0", {"start": v(129.2, -0.93) * mm, "mid": v(129.76, -1.16) * mm, "end": v(129.99, -1.72) * mm});
            skArc(sketch, "E63.190.3.0", {"start": v(116.7, 11.57) * mm, "mid": v(117.26, 11.34) * mm, "end": v(117.49, 10.78) * mm});
            skArc(sketch, "E63.194.3.0", {"start": v(117.49, -6.93) * mm, "mid": v(117.4, -6.72) * mm, "end": v(117.18, -6.63) * mm});
            skLineSegment(sketch, "E63.198.3.0", {"start": v(123.63, 1.57) * mm, "end": v(123.63, 2.7) * mm});
            skArc(sketch, "E63.201.3.0", {"start": v(126.76, 7.07) * mm, "mid": v(127.67, 7.25) * mm, "end": v(128.19, 6.48) * mm});
            skArc(sketch, "E63.205.3.0", {"start": v(128.19, 4.37) * mm, "mid": v(128.28, 4.16) * mm, "end": v(128.5, 4.07) * mm});
            skLineSegment(sketch, "E63.209.3.0", {"start": v(128.5, 4.07) * mm, "end": v(129.2, 4.07) * mm});
            skArc(sketch, "E63.212.3.0", {"start": v(129.2, 4.07) * mm, "mid": v(129.76, 4.3) * mm, "end": v(129.99, 4.86) * mm});
            skArc(sketch, "E63.216.3.0", {"start": v(123.28, 11.57) * mm, "mid": v(122.72, 11.34) * mm, "end": v(122.49, 10.78) * mm});
            skArc(sketch, "E63.220.3.0", {"start": v(123.28, -8.43) * mm, "mid": v(122.72, -8.2) * mm, "end": v(122.49, -7.64) * mm});
            skArc(sketch, "E63.224.3.0", {"start": v(128.19, -1.23) * mm, "mid": v(128.28, -1.02) * mm, "end": v(128.5, -0.93) * mm});
            skLineSegment(sketch, "E63.228.3.0", {"start": v(117.49, -7.64) * mm, "end": v(117.49, -6.93) * mm});
            skLineSegment(sketch, "E63.231.3.0", {"start": v(121.12, -2.07) * mm, "end": v(119.99, -2.07) * mm});
            skArc(sketch, "E63.234.3.0", {"start": v(122.49, -6.93) * mm, "mid": v(122.58, -6.72) * mm, "end": v(122.8, -6.63) * mm});
            skLineSegment(sketch, "E63.238.3.0", {"start": v(111.48, 4.07) * mm, "end": v(110.78, 4.07) * mm});
            skLineSegment(sketch, "E63.241.3.0", {"start": v(122.49, -7.64) * mm, "end": v(122.49, -6.93) * mm});
            skLineSegment(sketch, "E63.244.3.0", {"start": v(121.12, 5.21) * mm, "end": v(119.99, 5.21) * mm});
            skArc(sketch, "E63.247.3.0", {"start": v(115.08, 9.77) * mm, "mid": v(114.3, 9.25) * mm, "end": v(114.49, 8.34) * mm});
            skArc(sketch, "E63.251.3.0", {"start": v(111.79, 4.37) * mm, "mid": v(111.7, 4.16) * mm, "end": v(111.48, 4.07) * mm});
            skLineSegment(sketch, "E63.255.3.0", {"start": v(123.63, 1.57) * mm, "end": v(123.63, 0.44) * mm});
            skArc(sketch, "E63.258.3.0", {"start": v(117.49, 10.07) * mm, "mid": v(117.4, 9.86) * mm, "end": v(117.18, 9.77) * mm});
            skLineSegment(sketch, "E63.262.3.0", {"start": v(128.5, -0.93) * mm, "end": v(129.2, -0.93) * mm});
            skArc(sketch, "E63.265.3.0", {"start": v(122.49, 10.07) * mm, "mid": v(122.58, 9.86) * mm, "end": v(122.8, 9.77) * mm});
            skLineSegment(sketch, "E63.269.3.0", {"start": v(122.49, 10.78) * mm, "end": v(122.49, 10.07) * mm});
            skLineSegment(sketch, "E63.272.3.0", {"start": v(117.49, 10.78) * mm, "end": v(117.49, 10.07) * mm});
            skArc(sketch, "E63.0.4.0", {"start": v(164.9, -6.1) * mm, "mid": v(165.67, -5.6) * mm, "end": v(165.49, -4.68) * mm});
            skArc(sketch, "E63.4.4.0", {"start": v(156.34, 3.22) * mm, "mid": v(156.11, 4.37) * mm, "end": v(155.46, 5.34) * mm});
            skLineSegment(sketch, "E63.8.4.0", {"start": v(159.99, 2.1) * mm, "end": v(159.99, 12.8) * mm, "construction": true});
            skLineSegment(sketch, "E63.11.4.0", {"start": v(149.99, -1.2) * mm, "end": v(149.99, -5.9) * mm});
            skLineSegment(sketch, "E63.14.4.0", {"start": v(167.97, -7.9) * mm, "end": v(163.27, -7.9) * mm});
            skLineSegment(sketch, "E63.17.4.0", {"start": v(152, -7.9) * mm, "end": v(156.7, -7.9) * mm});
            skArc(sketch, "E63.20.4.0", {"start": v(163.63, 0.96) * mm, "mid": v(163.86, -0.18) * mm, "end": v(164.5, -1.16) * mm});
            skLineSegment(sketch, "E63.24.4.0", {"start": v(154.49, -4.68) * mm, "end": v(156.74, -2.43) * mm});
            skLineSegment(sketch, "E63.27.4.0", {"start": v(159.99, 2.1) * mm, "end": v(172.4, 2.1) * mm, "construction": true});
            skArc(sketch, "E63.30.4.0", {"start": v(153.21, -3.4) * mm, "mid": v(152.3, -3.59) * mm, "end": v(151.79, -2.82) * mm});
            skLineSegment(sketch, "E63.34.4.0", {"start": v(165.49, -4.68) * mm, "end": v(163.24, -2.43) * mm});
            skArc(sketch, "E63.37.4.0", {"start": v(163.24, -2.43) * mm, "mid": v(162.26, -1.78) * mm, "end": v(161.12, -1.55) * mm});
            skArc(sketch, "E63.41.4.0", {"start": v(156.74, 6.62) * mm, "mid": v(157.7, 5.97) * mm, "end": v(158.86, 5.74) * mm});
            skLineSegment(sketch, "E63.45.4.0", {"start": v(169.99, -1.2) * mm, "end": v(169.99, -5.9) * mm});
            skLineSegment(sketch, "E63.48.4.0", {"start": v(149.99, 5.38) * mm, "end": v(149.99, 10.08) * mm});
            skLineSegment(sketch, "E63.51.4.0", {"start": v(159.99, 2.1) * mm, "end": v(167.97, 10.08) * mm, "construction": true});
            skLineSegment(sketch, "E63.54.4.0", {"start": v(155.46, -1.16) * mm, "end": v(153.21, -3.4) * mm});
            skArc(sketch, "E63.57.4.0", {"start": v(149.99, -5.9) * mm, "mid": v(150.58, -7.32) * mm, "end": v(152, -7.9) * mm});
            skLineSegment(sketch, "E63.61.4.0", {"start": v(157.18, -6.1) * mm, "end": v(155.08, -6.1) * mm});
            skCircle(sketch, "E63.64.4.0", {"center": v(159.99, 2.1) * mm, "radius": 2 * mm});
            skArc(sketch, "E63.66.4.0", {"start": v(156.74, -2.43) * mm, "mid": v(157.7, -1.78) * mm, "end": v(158.86, -1.55) * mm});
            skLineSegment(sketch, "E63.70.4.0", {"start": v(155.46, 5.34) * mm, "end": v(153.21, 7.6) * mm});
            skArc(sketch, "E63.73.4.0", {"start": v(169.99, -5.9) * mm, "mid": v(169.4, -7.32) * mm, "end": v(167.97, -7.9) * mm});
            skLineSegment(sketch, "E63.77.4.0", {"start": v(162.8, -6.1) * mm, "end": v(164.9, -6.1) * mm});
            skLineSegment(sketch, "E63.80.4.0", {"start": v(162.8, 10.3) * mm, "end": v(164.9, 10.3) * mm});
            skArc(sketch, "E63.83.4.0", {"start": v(164.9, 10.3) * mm, "mid": v(165.67, 9.78) * mm, "end": v(165.49, 8.87) * mm});
            skArc(sketch, "E63.87.4.0", {"start": v(163.63, 3.22) * mm, "mid": v(163.86, 4.37) * mm, "end": v(164.5, 5.34) * mm});
            skLineSegment(sketch, "E63.91.4.0", {"start": v(164.5, 5.34) * mm, "end": v(166.76, 7.6) * mm});
            skLineSegment(sketch, "E63.94.4.0", {"start": v(168.19, 7) * mm, "end": v(168.19, 4.9) * mm});
            skLineSegment(sketch, "E63.97.4.0", {"start": v(169.99, 5.38) * mm, "end": v(169.99, 10.08) * mm});
            skArc(sketch, "E63.100.4.0", {"start": v(169.99, 10.08) * mm, "mid": v(169.4, 11.5) * mm, "end": v(167.97, 12.1) * mm});
            skLineSegment(sketch, "E63.104.4.0", {"start": v(167.97, 12.1) * mm, "end": v(163.27, 12.1) * mm});
            skLineSegment(sketch, "E63.107.4.0", {"start": v(154.49, 8.87) * mm, "end": v(156.74, 6.62) * mm});
            skLineSegment(sketch, "E63.110.4.0", {"start": v(152, 12.1) * mm, "end": v(156.7, 12.1) * mm});
            skLineSegment(sketch, "E63.113.4.0", {"start": v(165.49, 8.87) * mm, "end": v(163.24, 6.62) * mm});
            skLineSegment(sketch, "E63.116.4.0", {"start": v(164.5, -1.16) * mm, "end": v(166.76, -3.4) * mm});
            skLineSegment(sketch, "E63.119.4.0", {"start": v(151.79, 7) * mm, "end": v(151.79, 4.9) * mm});
            skArc(sketch, "E63.122.4.0", {"start": v(149.99, 10.08) * mm, "mid": v(150.58, 11.5) * mm, "end": v(152, 12.1) * mm});
            skArc(sketch, "E63.126.4.0", {"start": v(163.24, 6.62) * mm, "mid": v(162.26, 5.97) * mm, "end": v(161.12, 5.74) * mm});
            skLineSegment(sketch, "E63.130.4.0", {"start": v(168.19, -2.82) * mm, "end": v(168.19, -0.71) * mm});
            skArc(sketch, "E63.133.4.0", {"start": v(153.21, 7.6) * mm, "mid": v(152.3, 7.77) * mm, "end": v(151.79, 7) * mm});
            skLineSegment(sketch, "E63.137.4.0", {"start": v(151.79, -2.82) * mm, "end": v(151.79, -0.71) * mm});
            skArc(sketch, "E63.140.4.0", {"start": v(156.34, 0.96) * mm, "mid": v(156.11, -0.18) * mm, "end": v(155.46, -1.16) * mm});
            skLineSegment(sketch, "E63.144.4.0", {"start": v(157.18, 10.3) * mm, "end": v(155.08, 10.3) * mm});
            skArc(sketch, "E63.147.4.0", {"start": v(155.08, -6.1) * mm, "mid": v(154.3, -5.6) * mm, "end": v(154.49, -4.68) * mm});
            skArc(sketch, "E63.151.4.0", {"start": v(151.79, -0.71) * mm, "mid": v(151.7, -0.5) * mm, "end": v(151.48, -0.4) * mm});
            skLineSegment(sketch, "E63.155.4.0", {"start": v(158.86, -1.55) * mm, "end": v(159.99, -1.55) * mm});
            skLineSegment(sketch, "E63.158.4.0", {"start": v(151.48, -0.4) * mm, "end": v(150.77, -0.4) * mm});
            skArc(sketch, "E63.161.4.0", {"start": v(150.77, 4.6) * mm, "mid": v(150.22, 4.82) * mm, "end": v(149.99, 5.38) * mm});
            skArc(sketch, "E63.165.4.0", {"start": v(156.7, -7.9) * mm, "mid": v(157.26, -7.68) * mm, "end": v(157.49, -7.12) * mm});
            skLineSegment(sketch, "E63.169.4.0", {"start": v(158.86, 5.74) * mm, "end": v(159.99, 5.74) * mm});
            skLineSegment(sketch, "E63.172.4.0", {"start": v(156.34, 2.1) * mm, "end": v(156.34, 3.22) * mm});
            skArc(sketch, "E63.175.4.0", {"start": v(150.77, -0.4) * mm, "mid": v(150.22, -0.64) * mm, "end": v(149.99, -1.2) * mm});
            skLineSegment(sketch, "E63.179.4.0", {"start": v(156.34, 2.1) * mm, "end": v(156.34, 0.96) * mm});
            skArc(sketch, "E63.182.4.0", {"start": v(166.76, -3.4) * mm, "mid": v(167.67, -3.59) * mm, "end": v(168.19, -2.82) * mm});
            skArc(sketch, "E63.186.4.0", {"start": v(169.2, -0.4) * mm, "mid": v(169.76, -0.64) * mm, "end": v(169.99, -1.2) * mm});
            skArc(sketch, "E63.190.4.0", {"start": v(156.7, 12.1) * mm, "mid": v(157.26, 11.86) * mm, "end": v(157.49, 11.3) * mm});
            skArc(sketch, "E63.194.4.0", {"start": v(157.49, -6.41) * mm, "mid": v(157.4, -6.2) * mm, "end": v(157.18, -6.1) * mm});
            skLineSegment(sketch, "E63.198.4.0", {"start": v(163.63, 2.1) * mm, "end": v(163.63, 3.22) * mm});
            skArc(sketch, "E63.201.4.0", {"start": v(166.76, 7.6) * mm, "mid": v(167.67, 7.77) * mm, "end": v(168.19, 7) * mm});
            skArc(sketch, "E63.205.4.0", {"start": v(168.19, 4.9) * mm, "mid": v(168.28, 4.68) * mm, "end": v(168.5, 4.6) * mm});
            skLineSegment(sketch, "E63.209.4.0", {"start": v(168.5, 4.6) * mm, "end": v(169.2, 4.6) * mm});
            skArc(sketch, "E63.212.4.0", {"start": v(169.2, 4.6) * mm, "mid": v(169.76, 4.82) * mm, "end": v(169.99, 5.38) * mm});
            skArc(sketch, "E63.216.4.0", {"start": v(163.27, 12.1) * mm, "mid": v(162.72, 11.86) * mm, "end": v(162.49, 11.3) * mm});
            skArc(sketch, "E63.220.4.0", {"start": v(163.27, -7.9) * mm, "mid": v(162.72, -7.68) * mm, "end": v(162.49, -7.12) * mm});
            skArc(sketch, "E63.224.4.0", {"start": v(168.19, -0.71) * mm, "mid": v(168.28, -0.5) * mm, "end": v(168.5, -0.4) * mm});
            skLineSegment(sketch, "E63.228.4.0", {"start": v(157.49, -7.12) * mm, "end": v(157.49, -6.41) * mm});
            skLineSegment(sketch, "E63.231.4.0", {"start": v(161.12, -1.55) * mm, "end": v(159.99, -1.55) * mm});
            skArc(sketch, "E63.234.4.0", {"start": v(162.49, -6.41) * mm, "mid": v(162.58, -6.2) * mm, "end": v(162.8, -6.1) * mm});
            skLineSegment(sketch, "E63.238.4.0", {"start": v(151.48, 4.6) * mm, "end": v(150.77, 4.6) * mm});
            skLineSegment(sketch, "E63.241.4.0", {"start": v(162.49, -7.12) * mm, "end": v(162.49, -6.41) * mm});
            skLineSegment(sketch, "E63.244.4.0", {"start": v(161.12, 5.74) * mm, "end": v(159.99, 5.74) * mm});
            skArc(sketch, "E63.247.4.0", {"start": v(155.08, 10.3) * mm, "mid": v(154.3, 9.78) * mm, "end": v(154.49, 8.87) * mm});
            skArc(sketch, "E63.251.4.0", {"start": v(151.79, 4.9) * mm, "mid": v(151.7, 4.68) * mm, "end": v(151.48, 4.6) * mm});
            skLineSegment(sketch, "E63.255.4.0", {"start": v(163.63, 2.1) * mm, "end": v(163.63, 0.96) * mm});
            skArc(sketch, "E63.258.4.0", {"start": v(157.49, 10.6) * mm, "mid": v(157.4, 10.38) * mm, "end": v(157.18, 10.3) * mm});
            skLineSegment(sketch, "E63.262.4.0", {"start": v(168.5, -0.4) * mm, "end": v(169.2, -0.4) * mm});
            skArc(sketch, "E63.265.4.0", {"start": v(162.49, 10.6) * mm, "mid": v(162.58, 10.38) * mm, "end": v(162.8, 10.3) * mm});
            skLineSegment(sketch, "E63.269.4.0", {"start": v(162.49, 11.3) * mm, "end": v(162.49, 10.6) * mm});
            skLineSegment(sketch, "E63.272.4.0", {"start": v(157.49, 11.3) * mm, "end": v(157.49, 10.6) * mm});
            skArc(sketch, "E63.0.5.0", {"start": v(204.9, -5.58) * mm, "mid": v(205.66, -5.07) * mm, "end": v(205.48, -4.16) * mm});
            skArc(sketch, "E63.4.5.0", {"start": v(196.34, 3.75) * mm, "mid": v(196.1, 4.9) * mm, "end": v(195.46, 5.87) * mm});
            skLineSegment(sketch, "E63.8.5.0", {"start": v(199.98, 2.62) * mm, "end": v(199.98, 13.33) * mm, "construction": true});
            skLineSegment(sketch, "E63.11.5.0", {"start": v(189.98, -0.67) * mm, "end": v(189.98, -5.37) * mm});
            skLineSegment(sketch, "E63.14.5.0", {"start": v(207.97, -7.38) * mm, "end": v(203.27, -7.38) * mm});
            skLineSegment(sketch, "E63.17.5.0", {"start": v(192, -7.38) * mm, "end": v(196.7, -7.38) * mm});
            skArc(sketch, "E63.20.5.0", {"start": v(203.63, 1.49) * mm, "mid": v(203.86, 0.34) * mm, "end": v(204.5, -0.63) * mm});
            skLineSegment(sketch, "E63.24.5.0", {"start": v(194.48, -4.16) * mm, "end": v(196.73, -1.9) * mm});
            skLineSegment(sketch, "E63.27.5.0", {"start": v(199.98, 2.62) * mm, "end": v(212.4, 2.62) * mm, "construction": true});
            skArc(sketch, "E63.30.5.0", {"start": v(193.2, -2.88) * mm, "mid": v(192.3, -3.06) * mm, "end": v(191.78, -2.3) * mm});
            skLineSegment(sketch, "E63.34.5.0", {"start": v(205.48, -4.16) * mm, "end": v(203.23, -1.9) * mm});
            skArc(sketch, "E63.37.5.0", {"start": v(203.23, -1.9) * mm, "mid": v(202.26, -1.26) * mm, "end": v(201.11, -1.03) * mm});
            skArc(sketch, "E63.41.5.0", {"start": v(196.73, 7.14) * mm, "mid": v(197.7, 6.49) * mm, "end": v(198.85, 6.26) * mm});
            skLineSegment(sketch, "E63.45.5.0", {"start": v(209.98, -0.67) * mm, "end": v(209.98, -5.37) * mm});
            skLineSegment(sketch, "E63.48.5.0", {"start": v(189.98, 5.9) * mm, "end": v(189.98, 10.6) * mm});
            skLineSegment(sketch, "E63.51.5.0", {"start": v(199.98, 2.62) * mm, "end": v(207.97, 10.6) * mm, "construction": true});
            skLineSegment(sketch, "E63.54.5.0", {"start": v(195.46, -0.63) * mm, "end": v(193.2, -2.88) * mm});
            skArc(sketch, "E63.57.5.0", {"start": v(189.98, -5.37) * mm, "mid": v(190.57, -6.8) * mm, "end": v(192, -7.38) * mm});
            skLineSegment(sketch, "E63.61.5.0", {"start": v(197.18, -5.58) * mm, "end": v(195.07, -5.58) * mm});
            skCircle(sketch, "E63.64.5.0", {"center": v(199.98, 2.62) * mm, "radius": 2 * mm});
            skArc(sketch, "E63.66.5.0", {"start": v(196.73, -1.9) * mm, "mid": v(197.7, -1.26) * mm, "end": v(198.85, -1.03) * mm});
            skLineSegment(sketch, "E63.70.5.0", {"start": v(195.46, 5.87) * mm, "end": v(193.2, 8.12) * mm});
            skArc(sketch, "E63.73.5.0", {"start": v(209.98, -5.37) * mm, "mid": v(209.4, -6.8) * mm, "end": v(207.97, -7.38) * mm});
            skLineSegment(sketch, "E63.77.5.0", {"start": v(202.79, -5.58) * mm, "end": v(204.9, -5.58) * mm});
            skLineSegment(sketch, "E63.80.5.0", {"start": v(202.79, 10.82) * mm, "end": v(204.9, 10.82) * mm});
            skArc(sketch, "E63.83.5.0", {"start": v(204.9, 10.82) * mm, "mid": v(205.66, 10.3) * mm, "end": v(205.48, 9.39) * mm});
            skArc(sketch, "E63.87.5.0", {"start": v(203.63, 3.75) * mm, "mid": v(203.86, 4.9) * mm, "end": v(204.5, 5.87) * mm});
            skLineSegment(sketch, "E63.91.5.0", {"start": v(204.5, 5.87) * mm, "end": v(206.76, 8.12) * mm});
            skLineSegment(sketch, "E63.94.5.0", {"start": v(208.18, 7.53) * mm, "end": v(208.18, 5.42) * mm});
            skLineSegment(sketch, "E63.97.5.0", {"start": v(209.98, 5.9) * mm, "end": v(209.98, 10.6) * mm});
            skArc(sketch, "E63.100.5.0", {"start": v(209.98, 10.6) * mm, "mid": v(209.4, 12.03) * mm, "end": v(207.97, 12.62) * mm});
            skLineSegment(sketch, "E63.104.5.0", {"start": v(207.97, 12.62) * mm, "end": v(203.27, 12.62) * mm});
            skLineSegment(sketch, "E63.107.5.0", {"start": v(194.48, 9.39) * mm, "end": v(196.73, 7.14) * mm});
            skLineSegment(sketch, "E63.110.5.0", {"start": v(192, 12.62) * mm, "end": v(196.7, 12.62) * mm});
            skLineSegment(sketch, "E63.113.5.0", {"start": v(205.48, 9.39) * mm, "end": v(203.23, 7.14) * mm});
            skLineSegment(sketch, "E63.116.5.0", {"start": v(204.5, -0.63) * mm, "end": v(206.76, -2.88) * mm});
            skLineSegment(sketch, "E63.119.5.0", {"start": v(191.78, 7.53) * mm, "end": v(191.78, 5.42) * mm});
            skArc(sketch, "E63.122.5.0", {"start": v(189.98, 10.6) * mm, "mid": v(190.57, 12.03) * mm, "end": v(192, 12.62) * mm});
            skArc(sketch, "E63.126.5.0", {"start": v(203.23, 7.14) * mm, "mid": v(202.26, 6.49) * mm, "end": v(201.11, 6.26) * mm});
            skLineSegment(sketch, "E63.130.5.0", {"start": v(208.18, -2.3) * mm, "end": v(208.18, -0.19) * mm});
            skArc(sketch, "E63.133.5.0", {"start": v(193.2, 8.12) * mm, "mid": v(192.3, 8.3) * mm, "end": v(191.78, 7.53) * mm});
            skLineSegment(sketch, "E63.137.5.0", {"start": v(191.78, -2.3) * mm, "end": v(191.78, -0.19) * mm});
            skArc(sketch, "E63.140.5.0", {"start": v(196.34, 1.49) * mm, "mid": v(196.1, 0.34) * mm, "end": v(195.46, -0.63) * mm});
            skLineSegment(sketch, "E63.144.5.0", {"start": v(197.18, 10.82) * mm, "end": v(195.07, 10.82) * mm});
            skArc(sketch, "E63.147.5.0", {"start": v(195.07, -5.58) * mm, "mid": v(194.3, -5.07) * mm, "end": v(194.48, -4.16) * mm});
            skArc(sketch, "E63.151.5.0", {"start": v(191.78, -0.19) * mm, "mid": v(191.7, 0.03) * mm, "end": v(191.48, 0.12) * mm});
            skLineSegment(sketch, "E63.155.5.0", {"start": v(198.85, -1.03) * mm, "end": v(199.98, -1.03) * mm});
            skLineSegment(sketch, "E63.158.5.0", {"start": v(191.48, 0.12) * mm, "end": v(190.77, 0.12) * mm});
            skArc(sketch, "E63.161.5.0", {"start": v(190.77, 5.12) * mm, "mid": v(190.21, 5.35) * mm, "end": v(189.98, 5.9) * mm});
            skArc(sketch, "E63.165.5.0", {"start": v(196.7, -7.38) * mm, "mid": v(197.25, -7.15) * mm, "end": v(197.48, -6.6) * mm});
            skLineSegment(sketch, "E63.169.5.0", {"start": v(198.85, 6.26) * mm, "end": v(199.98, 6.26) * mm});
            skLineSegment(sketch, "E63.172.5.0", {"start": v(196.34, 2.62) * mm, "end": v(196.34, 3.75) * mm});
            skArc(sketch, "E63.175.5.0", {"start": v(190.77, 0.12) * mm, "mid": v(190.21, -0.11) * mm, "end": v(189.98, -0.67) * mm});
            skLineSegment(sketch, "E63.179.5.0", {"start": v(196.34, 2.62) * mm, "end": v(196.34, 1.49) * mm});
            skArc(sketch, "E63.182.5.0", {"start": v(206.76, -2.88) * mm, "mid": v(207.67, -3.06) * mm, "end": v(208.18, -2.3) * mm});
            skArc(sketch, "E63.186.5.0", {"start": v(209.2, 0.12) * mm, "mid": v(209.75, -0.11) * mm, "end": v(209.98, -0.67) * mm});
            skArc(sketch, "E63.190.5.0", {"start": v(196.7, 12.62) * mm, "mid": v(197.25, 12.39) * mm, "end": v(197.48, 11.83) * mm});
            skArc(sketch, "E63.194.5.0", {"start": v(197.48, -5.89) * mm, "mid": v(197.4, -5.67) * mm, "end": v(197.18, -5.58) * mm});
            skLineSegment(sketch, "E63.198.5.0", {"start": v(203.63, 2.62) * mm, "end": v(203.63, 3.75) * mm});
            skArc(sketch, "E63.201.5.0", {"start": v(206.76, 8.12) * mm, "mid": v(207.67, 8.3) * mm, "end": v(208.18, 7.53) * mm});
            skArc(sketch, "E63.205.5.0", {"start": v(208.18, 5.42) * mm, "mid": v(208.27, 5.2) * mm, "end": v(208.49, 5.12) * mm});
            skLineSegment(sketch, "E63.209.5.0", {"start": v(208.49, 5.12) * mm, "end": v(209.2, 5.12) * mm});
            skArc(sketch, "E63.212.5.0", {"start": v(209.2, 5.12) * mm, "mid": v(209.75, 5.35) * mm, "end": v(209.98, 5.9) * mm});
            skArc(sketch, "E63.216.5.0", {"start": v(203.27, 12.62) * mm, "mid": v(202.71, 12.39) * mm, "end": v(202.48, 11.83) * mm});
            skArc(sketch, "E63.220.5.0", {"start": v(203.27, -7.38) * mm, "mid": v(202.71, -7.15) * mm, "end": v(202.48, -6.6) * mm});
            skArc(sketch, "E63.224.5.0", {"start": v(208.18, -0.19) * mm, "mid": v(208.27, 0.03) * mm, "end": v(208.49, 0.12) * mm});
            skLineSegment(sketch, "E63.228.5.0", {"start": v(197.48, -6.6) * mm, "end": v(197.48, -5.89) * mm});
            skLineSegment(sketch, "E63.231.5.0", {"start": v(201.11, -1.03) * mm, "end": v(199.98, -1.03) * mm});
            skArc(sketch, "E63.234.5.0", {"start": v(202.48, -5.89) * mm, "mid": v(202.57, -5.67) * mm, "end": v(202.79, -5.58) * mm});
            skLineSegment(sketch, "E63.238.5.0", {"start": v(191.48, 5.12) * mm, "end": v(190.77, 5.12) * mm});
            skLineSegment(sketch, "E63.241.5.0", {"start": v(202.48, -6.6) * mm, "end": v(202.48, -5.89) * mm});
            skLineSegment(sketch, "E63.244.5.0", {"start": v(201.11, 6.26) * mm, "end": v(199.98, 6.26) * mm});
            skArc(sketch, "E63.247.5.0", {"start": v(195.07, 10.82) * mm, "mid": v(194.3, 10.3) * mm, "end": v(194.48, 9.39) * mm});
            skArc(sketch, "E63.251.5.0", {"start": v(191.78, 5.42) * mm, "mid": v(191.7, 5.2) * mm, "end": v(191.48, 5.12) * mm});
            skLineSegment(sketch, "E63.255.5.0", {"start": v(203.63, 2.62) * mm, "end": v(203.63, 1.49) * mm});
            skArc(sketch, "E63.258.5.0", {"start": v(197.48, 11.12) * mm, "mid": v(197.4, 10.9) * mm, "end": v(197.18, 10.82) * mm});
            skLineSegment(sketch, "E63.262.5.0", {"start": v(208.49, 0.12) * mm, "end": v(209.2, 0.12) * mm});
            skArc(sketch, "E63.265.5.0", {"start": v(202.48, 11.12) * mm, "mid": v(202.57, 10.9) * mm, "end": v(202.79, 10.82) * mm});
            skLineSegment(sketch, "E63.269.5.0", {"start": v(202.48, 11.83) * mm, "end": v(202.48, 11.12) * mm});
            skLineSegment(sketch, "E63.272.5.0", {"start": v(197.48, 11.83) * mm, "end": v(197.48, 11.12) * mm});
            skSolve(sketch);
        }
        {
            var Q0;
            Q0=makeQuery(id+"F0.imprint","IMPRINT",FACE,{"disambiguationData":[TD([[makeQuery(id+"F0.imprint","IMPRINT",EDGE,{"derivedFrom":sQuery(id+"F0.wireOp",EDGE,"E0.0.53")}),1.0]])]});
            extrude(context, id + "F1", {"entities" : qUnion([Q0]), "endBound" : BoundingType.SYMMETRIC, "depth" : 350 * mm});
        }
        {
            var Q0;
            Q0=makeQuery(id+"F0.imprint","IMPRINT",FACE,{"disambiguationData":[TD([[makeQuery(id+"F0.imprint","IMPRINT",EDGE,{"derivedFrom":sQuery(id+"F0.wireOp",EDGE,"E62.1.0.0")}),-1.0]])]});
            extrude(context, id + "F2", {"entities" : qUnion([Q0]), "endBound" : BoundingType.SYMMETRIC, "depth" : 325 * mm});
        }
        {
            var Q0;
            Q0=makeQuery(id+"F0.imprint","IMPRINT",FACE,{"disambiguationData":[TD([[makeQuery(id+"F0.imprint","IMPRINT",EDGE,{"derivedFrom":sQuery(id+"F0.wireOp",EDGE,"E62.2.0.0")}),-1.0]])]});
            extrude(context, id + "F3", {"entities" : qUnion([Q0]), "endBound" : BoundingType.SYMMETRIC, "depth" : 457.2 * mm});
        }
        {
            var Q0;
            Q0=makeQuery(id+"F0.imprint","IMPRINT",FACE,{"disambiguationData":[TD([[makeQuery(id+"F0.imprint","IMPRINT",EDGE,{"derivedFrom":sQuery(id+"F0.wireOp",EDGE,"E63.0.3.0")}),-1.0]])]});
            extrude(context, id + "F4", {"entities" : qUnion([Q0]), "depth" : 175 * mm});
        }
    });
